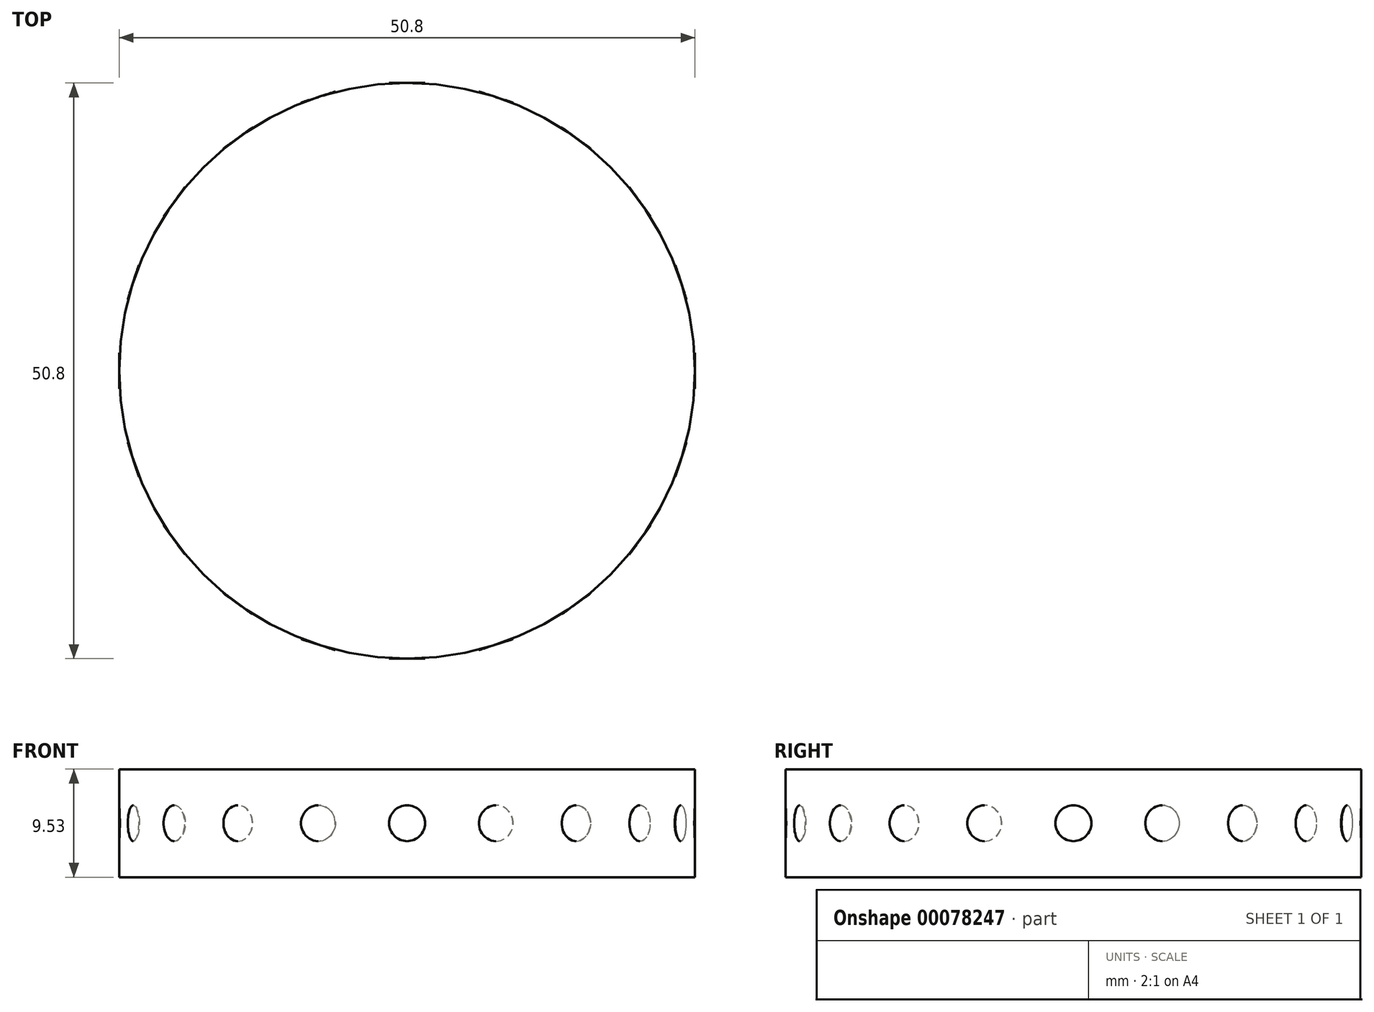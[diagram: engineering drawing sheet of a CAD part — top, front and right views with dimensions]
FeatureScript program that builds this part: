
annotation { "Feature Type Name" : "Feature", "Feature Type Description" : "" }
export const myFeature = defineFeature(function(context is Context, id is Id, definition is map)
    precondition{}
    {
        {
            var Q0;
            Q0=qCreatedBy(makeId("Top.planeOp"),FACE);
            var sketch = newSketch(context, id + "F0", { "sketchPlane" : qUnion([Q0])});
            skCircle(sketch, "E0", {"center": v(0, 0) * mm, "radius": 25.4 * mm, "construction": true});
            skCircle(sketch, "E1", {"center": v(0, -25.4) * mm, "radius": 25.4 * mm});
            skSolve(sketch);
        }
        {
            var Q0;
            Q0 = qSketchRegion(id + "F0", true);
            extrude(context, id + "F1", {"entities" : qUnion([Q0]), "depth" : 9.52 * mm});
        }
        {
            var Q0;
            Q0=qCreatedBy(makeId("Front.planeOp"),FACE);
            var sketch = newSketch(context, id + "F2", { "sketchPlane" : qUnion([Q0])});
            skLineSegment(sketch, "E2", {"start": v(0, 0) * mm, "end": v(0, 9.53) * mm, "construction": true});
            skPoint(sketch, "E3", {"position": v(0, 4.76) * mm});
            skCircle(sketch, "E4", {"center": v(0, 4.76) * mm, "radius": 1.58 * mm});
            skSolve(sketch);
        }
        {
            var Q0;
            Q0 = qSketchRegion(id + "F2", true);
            extrude(context, id + "F3", {"entities" : qUnion([Q0]), "operationType" : NewBodyOperationType.ADD, "depth" : 5 * mm});
        }
        {
            var Q0;
            Q0=makeQuery(id+"F1.opExtrude","SWEPT_BODY",BODY,{"disambiguationData":[OSD([sQuery(id+"F0.wireOp",EDGE,"E1")])]});
            var Q1;
            Q1=makeQuery(id+"F1.opExtrude","CAP_EDGE",EDGE,{"disambiguationData":[OSD([sQuery(id+"F0.wireOp",EDGE,"E1")])],"isStart":false});
            circularPattern(context, id + "F4", {"entities" : qUnion([Q0]), "axis" : qUnion([Q1]), "angle" : 360 * degree, "instanceCount" : 20, "equalSpace" : true});
        }
    });
